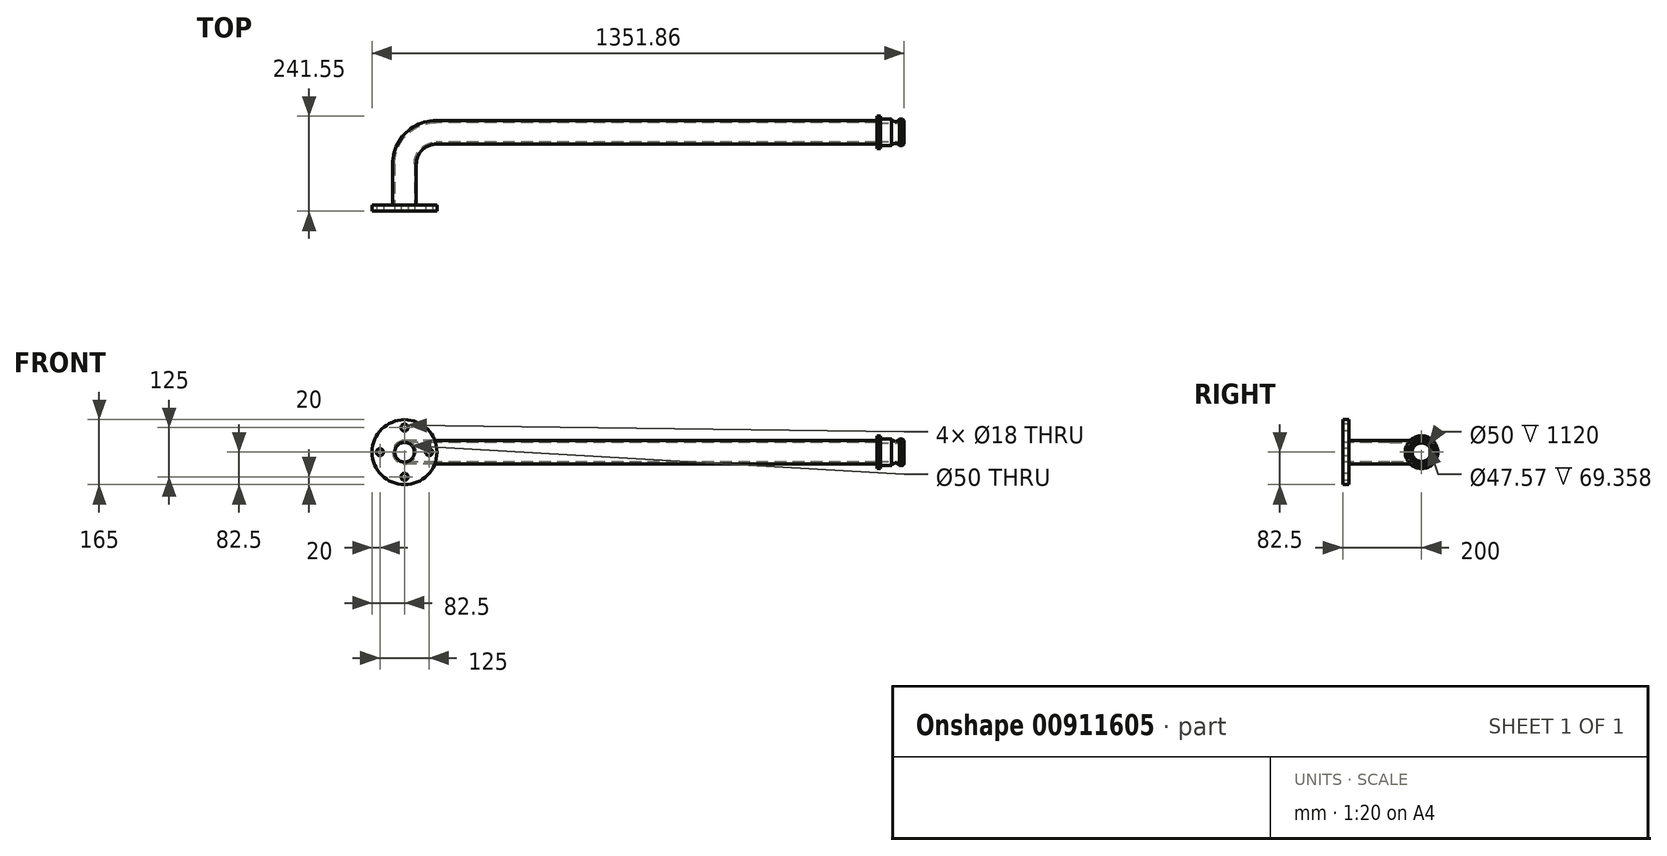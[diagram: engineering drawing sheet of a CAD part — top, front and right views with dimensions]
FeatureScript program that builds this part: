
annotation { "Feature Type Name" : "Feature", "Feature Type Description" : "" }
export const myFeature = defineFeature(function(context is Context, id is Id, definition is map)
    precondition{}
    {
        {
            var Q0;
            Q0=qCreatedBy(makeId("Top.planeOp"),FACE);
            var sketch = newSketch(context, id + "F0", { "sketchPlane" : qUnion([Q0])});
            skLineSegment(sketch, "E0", {"start": v(0, 0) * mm, "end": v(-1120, 0) * mm});
            skLineSegment(sketch, "E1", {"start": v(-1200, -80) * mm, "end": v(-1200, -200) * mm});
            skPoint(sketch, "E2.visualSharp", {"position": v(-1200, 0) * mm});
            skArc(sketch, "E2.filletArc", {"start": v(-1120, 0) * mm, "mid": v(-1176.57, -23.43) * mm, "end": v(-1200, -80) * mm});
            skSolve(sketch);
        }
        {
            var Q0;
            Q0=qCreatedBy(makeId("Right.planeOp"),FACE);
            var sketch = newSketch(context, id + "F1", { "sketchPlane" : qUnion([Q0])});
            skCircle(sketch, "E3", {"center": v(0, 0) * mm, "radius": 25 * mm});
            skCircle(sketch, "E4", {"center": v(0, 0) * mm, "radius": 30 * mm});
            skSolve(sketch);
        }
        {
            var Q0;
            Q0=makeQuery(id+"F1.imprint","IMPRINT",FACE,{"disambiguationData":[TD([[makeQuery(id+"F1.imprint","IMPRINT",EDGE,{"derivedFrom":sQuery(id+"F1.wireOp",EDGE,"E3")}),-1.0]])]});
            var Q1;
            Q1=sQuery(id+"F0.wireOp",EDGE,"E0");
            var Q2;
            Q2=sQuery(id+"F0.wireOp",EDGE,"E2.filletArc");
            var Q3;
            Q3=sQuery(id+"F0.wireOp",EDGE,"E1");
            sweep(context, id + "F2", {"profiles" : qUnion([Q0]), "path" : qUnion([Q1, Q2, Q3])});
        }
        {
            var Q0;
            Q0=makeQuery(id+"F2.opSweep","CAP_FACE",FACE,{"disambiguationData":[OSD([sQuery(id+"F0.wireOp",VERTEX,"E1.end"),sQuery(id+"F1.wireOp",EDGE,"E3"),sQuery(id+"F1.wireOp",EDGE,"E4")])],"isStart":false});
            var sketch = newSketch(context, id + "F3", { "sketchPlane" : qUnion([Q0])});
            skCircle(sketch, "E5", {"center": v(-1200, 0) * mm, "radius": 82.5 * mm});
            skCircle(sketch, "E6", {"center": v(-1200, 62.5) * mm, "radius": 9 * mm});
            skCircle(sketch, "E7.0", {"center": v(-1200, 0) * mm, "radius": 25 * mm});
            skCircle(sketch, "E8.1.0", {"center": v(-1262.5, 0) * mm, "radius": 9 * mm});
            skCircle(sketch, "E8.2.0", {"center": v(-1200, -62.5) * mm, "radius": 9 * mm});
            skCircle(sketch, "E8.3.0", {"center": v(-1137.5, 0) * mm, "radius": 9 * mm});
            skSolve(sketch);
        }
        {
            var Q0;
            Q0=qSketchRegion(id+"F3",true);
            extrude(context, id + "F4", {"entities" : qUnion([Q0]), "operationType" : NewBodyOperationType.ADD, "oppositeDirection" : true, "depth" : 15 * mm, "offsetDistance" : 25 * mm});
        }
        {
            var Q0;
            Q0=qCreatedBy(makeId("Front.planeOp"),FACE);
            var sketch = newSketch(context, id + "F5", { "sketchPlane" : qUnion([Q0])});
            skLineSegment(sketch, "E9", {"start": v(-1120, 30) * mm, "end": v(0, 30) * mm});
            skLineSegment(sketch, "E10.0", {"start": v(0, -30) * mm, "end": v(0, 30) * mm});
            skLineSegment(sketch, "E11", {"start": v(0, -30) * mm, "end": v(-1120, -30) * mm});
            skLineSegment(sketch, "E12", {"start": v(0, 30) * mm, "end": v(0, 41.55) * mm});
            skLineSegment(sketch, "E13", {"start": v(0, 41.55) * mm, "end": v(9.2, 41.55) * mm});
            skLineSegment(sketch, "E14", {"start": v(9.2, 41.55) * mm, "end": v(9.2, 33.63) * mm});
            skLineSegment(sketch, "E15", {"start": v(9.2, 33.63) * mm, "end": v(37.17, 33.63) * mm});
            skArc(sketch, "E16", {"start": v(37.17, 33.63) * mm, "mid": v(47.29, 27.82) * mm, "end": v(57.4, 33.63) * mm});
            skLineSegment(sketch, "E17", {"start": v(57.4, 33.63) * mm, "end": v(65.31, 33.63) * mm});
            skLineSegment(sketch, "E18", {"start": v(65.31, 33.63) * mm, "end": v(69.36, 30.12) * mm});
            skLineSegment(sketch, "E19", {"start": v(69.36, 30.12) * mm, "end": v(69.36, 23.79) * mm});
            skLineSegment(sketch, "E20", {"start": v(69.36, 23.79) * mm, "end": v(0, 23.79) * mm});
            skLineSegment(sketch, "E21", {"start": v(0, 23.79) * mm, "end": v(0, 30) * mm});
            skSolve(sketch);
        }
        {
            var Q0;
            Q0=makeQuery(id+"F5.imprint","IMPRINT",FACE,{"disambiguationData":[TD([[makeQuery(id+"F5.imprint","IMPRINT",EDGE,{"derivedFrom":sQuery(id+"F5.wireOp",EDGE,"E12")}),-1.0]])]});
            var Q1;
            Q1=makeQuery(id+"F2.opSweep","SWEPT_FACE",FACE,{"disambiguationData":[OSD([sQuery(id+"F0.wireOp",EDGE,"E0"),sQuery(id+"F1.wireOp",EDGE,"E4")])]});
            revolve(context, id + "F6", {"operationType" : NewBodyOperationType.ADD, "surfaceOperationType" : NewSurfaceOperationType.NEW, "entities" : qUnion([Q0]), "axis" : qUnion([Q1]), "revolveType" : RevolveType.FULL});
        }
    });
